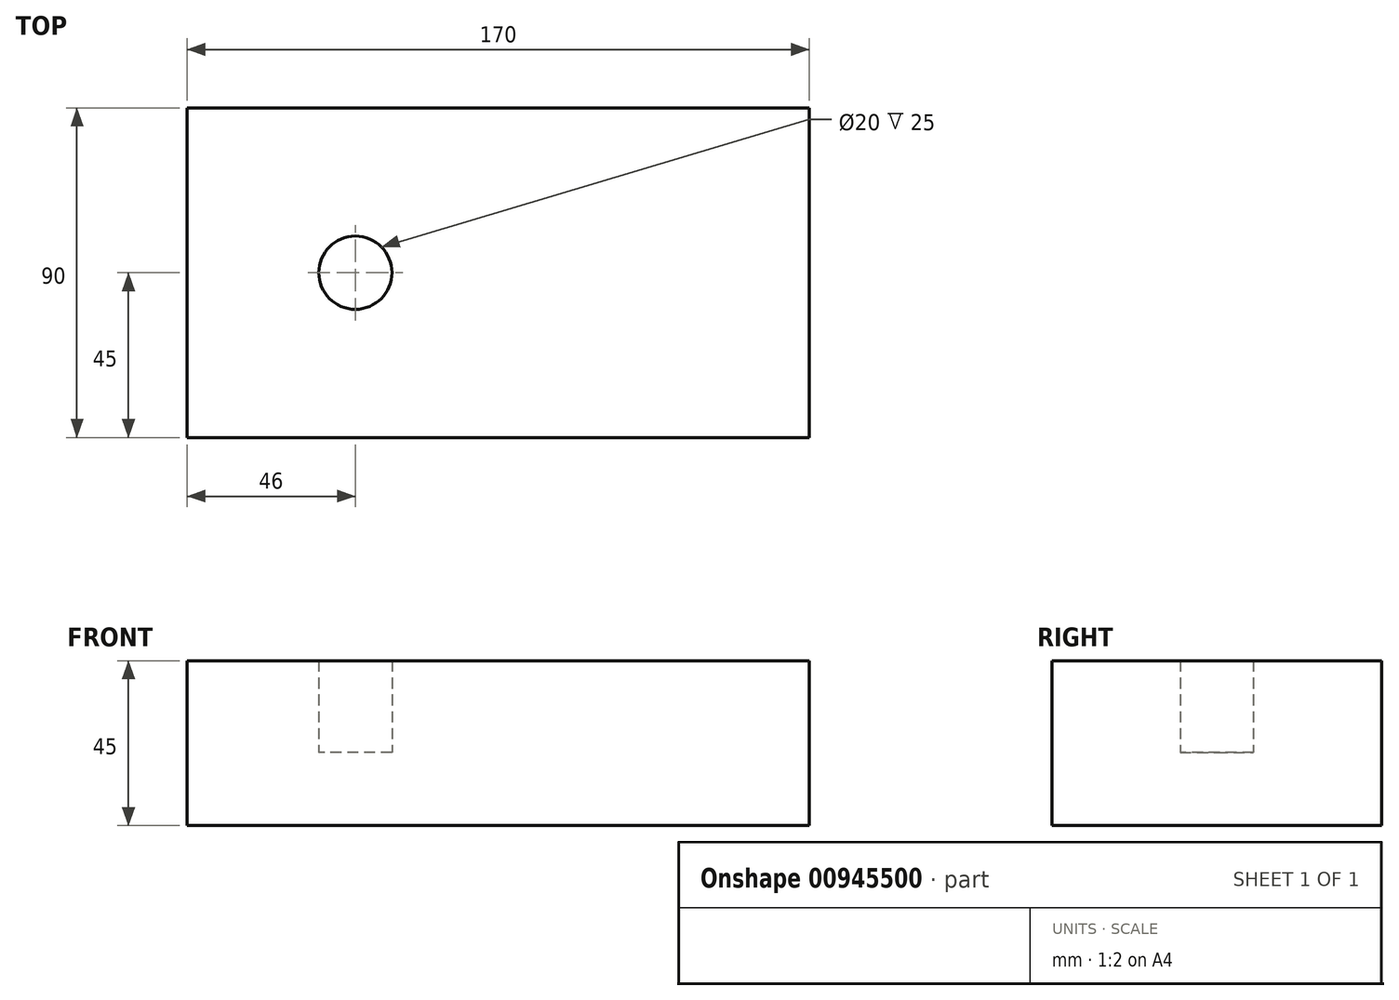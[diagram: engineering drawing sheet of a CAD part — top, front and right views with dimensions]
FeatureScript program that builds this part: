
annotation { "Feature Type Name" : "Feature", "Feature Type Description" : "" }
export const myFeature = defineFeature(function(context is Context, id is Id, definition is map)
    precondition{}
    {
        {
            var Q0;
            Q0=qCreatedBy(makeId("Top.planeOp"),FACE);
            var sketch = newSketch(context, id + "F0", { "sketchPlane" : qUnion([Q0])});
            skLineSegment(sketch, "E0.bottom", {"start": v(-85, 45) * mm, "end": v(85, 45) * mm});
            skLineSegment(sketch, "E0.top", {"start": v(-85, -45) * mm, "end": v(85, -45) * mm});
            skLineSegment(sketch, "E0.left", {"start": v(-85, 45) * mm, "end": v(-85, -45) * mm});
            skLineSegment(sketch, "E0.right", {"start": v(85, 45) * mm, "end": v(85, -45) * mm});
            skPoint(sketch, "E0.middle", {"position": v(0, 0) * mm});
            skSolve(sketch);
        }
        {
            var Q0;
            Q0=makeQuery(id+"F0.imprint","IMPRINT",FACE,{"disambiguationData":[TD([[makeQuery(id+"F0.imprint","IMPRINT",EDGE,{"derivedFrom":sQuery(id+"F0.wireOp",EDGE,"E0.bottom")}),-1.0]])]});
            extrude(context, id + "F1", {"entities" : qUnion([Q0]), "depth" : 20 * mm, "offsetDistance" : 25 * mm});
        }
        {
            var Q0;
            Q0=makeQuery(id+"F1.opExtrude","CAP_FACE",FACE,{"disambiguationData":[OSD([sQuery(id+"F0.wireOp",EDGE,"E0.bottom"),sQuery(id+"F0.wireOp",EDGE,"E0.top"),sQuery(id+"F0.wireOp",EDGE,"E0.left"),sQuery(id+"F0.wireOp",EDGE,"E0.right")])],"isStart":false});
            var sketch = newSketch(context, id + "F2", { "sketchPlane" : qUnion([Q0])});
            skLineSegment(sketch, "E1", {"start": v(-85, 0) * mm, "end": v(85, 0) * mm});
            skLineSegment(sketch, "E2", {"start": v(0, 0) * mm, "end": v(-39, 0) * mm});
            skLineSegment(sketch, "E3", {"start": v(0, 0) * mm, "end": v(39, 0) * mm});
            skCircle(sketch, "E4", {"center": v(-39, 0) * mm, "radius": 10 * mm});
            skCircle(sketch, "E5", {"center": v(39, 0) * mm, "radius": 10 * mm});
            skSolve(sketch);
        }
        {
            var Q0;
            {var subQ0=sQuery(id+"F2.wireOp",EDGE,"E1");var subQ1=makeQuery(id+"F2.imprint","IMPRINT",VERTEX,{"disambiguationData":[OD(2.0)],"derivedFrom":subQ0});Q0=makeQuery(id+"F2.imprint","IMPRINT",FACE,{"disambiguationData":[TD([[makeQuery(id+"F2.imprint","IMPRINT",EDGE,{"disambiguationData":[TD([[subQ1,-1.0]])],"derivedFrom":subQ0}),-1.0]])]});}
            var Q1;
            {var subQ0=sQuery(id+"F2.wireOp",EDGE,"E1");var subQ1=makeQuery(id+"F2.imprint","IMPRINT",VERTEX,{"disambiguationData":[OD(2.0)],"derivedFrom":subQ0});Q1=makeQuery(id+"F2.imprint","IMPRINT",FACE,{"disambiguationData":[TD([[makeQuery(id+"F2.imprint","IMPRINT",EDGE,{"disambiguationData":[TD([[subQ1,-1.0]])],"derivedFrom":subQ0}),1.0]])]});}
            var Q2;
            {var subQ1=sQuery(id+"F2.wireOp",EDGE,"E1");var subQ3=makeQuery(id+"F2.imprint","IMPRINT",VERTEX,{"disambiguationData":[OD(0.0)],"derivedFrom":subQ1});Q2=makeQuery(id+"F2.imprint","IMPRINT",FACE,{"disambiguationData":[TD([[makeQuery(id+"F2.imprint","IMPRINT",EDGE,{"disambiguationData":[TD([[subQ3,-1.0]])],"derivedFrom":subQ1}),1.0]])]});}
            var Q3;
            {var subQ1=sQuery(id+"F2.wireOp",EDGE,"E1");var subQ3=makeQuery(id+"F2.imprint","IMPRINT",VERTEX,{"disambiguationData":[OD(0.0)],"derivedFrom":subQ1});Q3=makeQuery(id+"F2.imprint","IMPRINT",FACE,{"disambiguationData":[TD([[makeQuery(id+"F2.imprint","IMPRINT",EDGE,{"disambiguationData":[TD([[subQ3,-1.0]])],"derivedFrom":subQ1}),-1.0]])]});}
            extrude(context, id + "F3", {"entities" : qUnion([Q0, Q1, Q2, Q3]), "operationType" : NewBodyOperationType.ADD, "depth" : 25 * mm, "offsetDistance" : 25 * mm});
        }
    });
